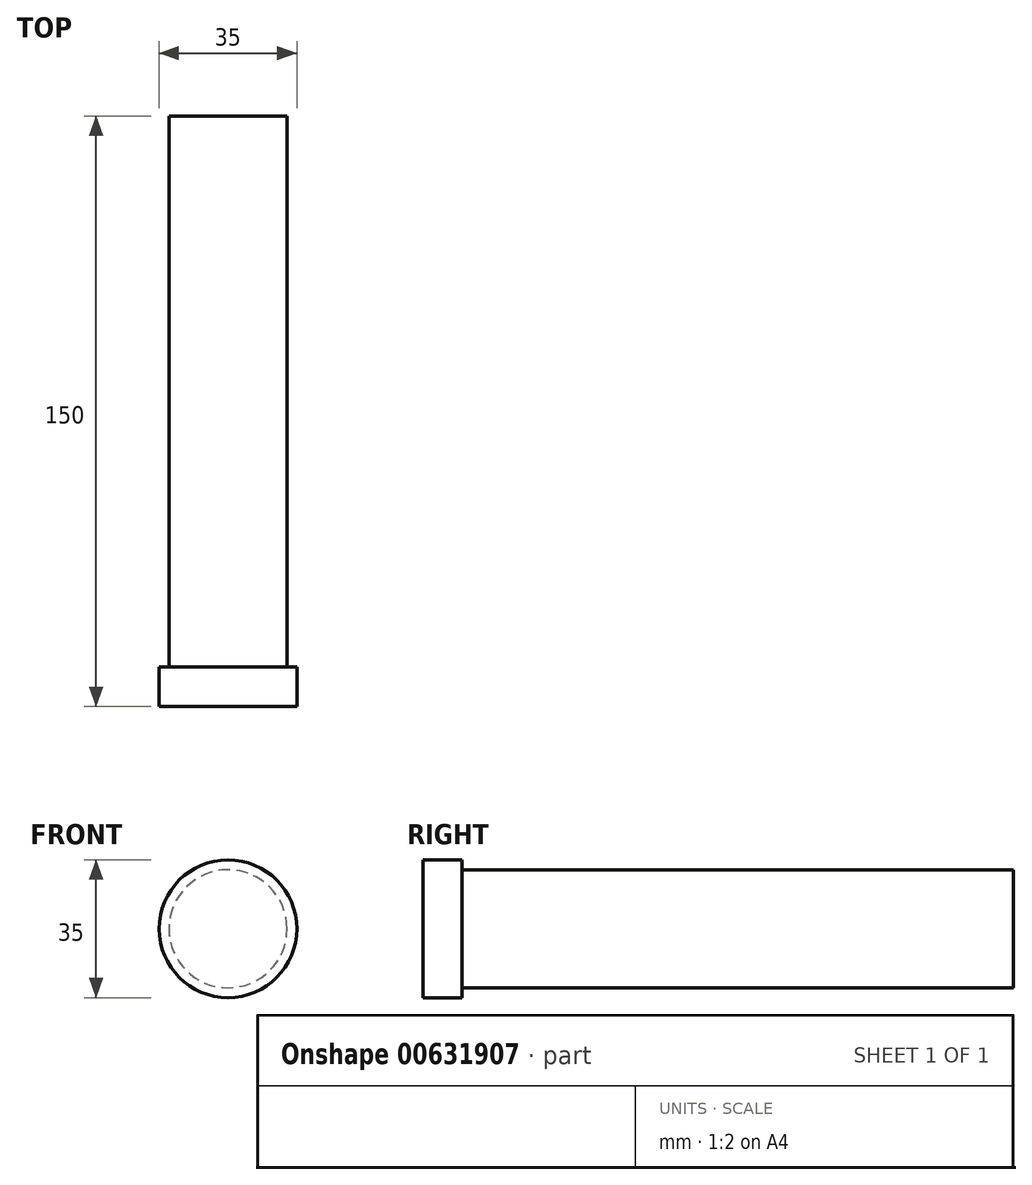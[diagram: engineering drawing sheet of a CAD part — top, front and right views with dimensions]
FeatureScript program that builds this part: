
annotation { "Feature Type Name" : "Feature", "Feature Type Description" : "" }
export const myFeature = defineFeature(function(context is Context, id is Id, definition is map)
    precondition{}
    {
        {
            var Q0;
            Q0=qCreatedBy(makeId("Front.planeOp"),FACE);
            var sketch = newSketch(context, id + "F0", { "sketchPlane" : qUnion([Q0])});
            skCircle(sketch, "E0", {"center": v(-39, 37.17) * mm, "radius": 15 * mm});
            skCircle(sketch, "E1", {"center": v(-39, 37.17) * mm, "radius": 17.5 * mm});
            skSolve(sketch);
        }
        {
            var Q0;
            Q0=makeQuery(id+"F0.imprint","IMPRINT",FACE,{"disambiguationData":[TD([[makeQuery(id+"F0.imprint","IMPRINT",EDGE,{"derivedFrom":sQuery(id+"F0.wireOp",EDGE,"E0")}),1.0]])]});
            extrude(context, id + "F1", {"entities" : qUnion([Q0]), "depth" : 140 * mm, "offsetDistance" : 25 * mm});
        }
        {
            var Q0;
            Q0=makeQuery(id+"F1.opExtrude","CAP_FACE",FACE,{"disambiguationData":[OSD([sQuery(id+"F0.wireOp",EDGE,"E0")])],"isStart":false});
            var sketch = newSketch(context, id + "F2", { "sketchPlane" : qUnion([Q0])});
            skCircle(sketch, "E2", {"center": v(-39, 37.17) * mm, "radius": 17.5 * mm});
            skSolve(sketch);
        }
        {
            var Q0;
            Q0=makeQuery(id+"F2.imprint","IMPRINT",FACE,{"disambiguationData":[TD([[makeQuery(id+"F2.imprint","IMPRINT",EDGE,{"derivedFrom":makeQuery(id+"F1.opExtrude","CAP_EDGE",EDGE,{"disambiguationData":[OSD([sQuery(id+"F0.wireOp",EDGE,"E0")])],"isStart":false})}),1.0]])]});
            var Q1;
            Q1=makeQuery(id+"F2.imprint","IMPRINT",FACE,{"disambiguationData":[TD([[makeQuery(id+"F2.imprint","IMPRINT",EDGE,{"derivedFrom":sQuery(id+"F2.wireOp",EDGE,"E2")}),1.0]])]});
            extrude(context, id + "F3", {"entities" : qUnion([Q0, Q1]), "operationType" : NewBodyOperationType.ADD, "depth" : 10 * mm, "offsetDistance" : 25 * mm});
        }
    });
